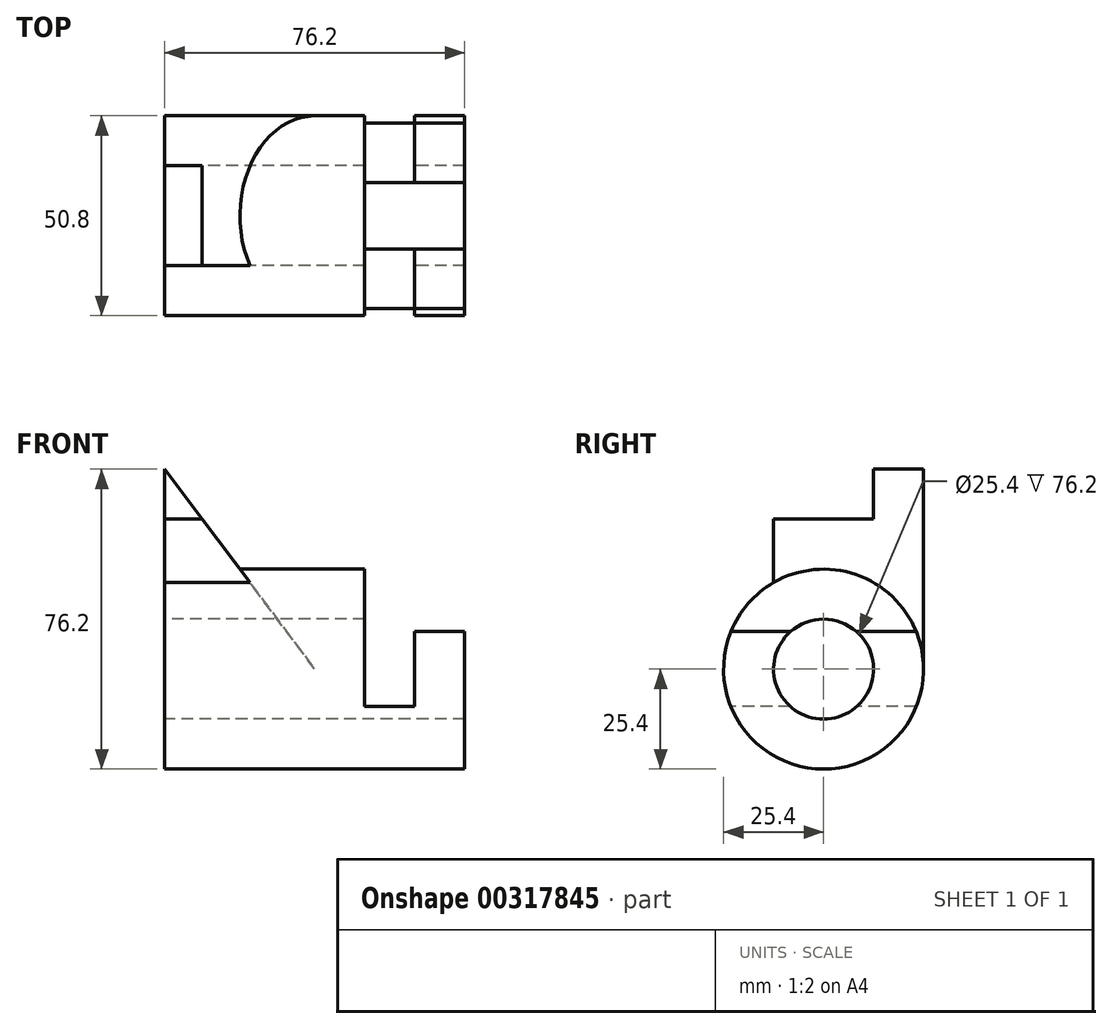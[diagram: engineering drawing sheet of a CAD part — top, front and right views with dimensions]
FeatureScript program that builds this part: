
annotation { "Feature Type Name" : "Feature", "Feature Type Description" : "" }
export const myFeature = defineFeature(function(context is Context, id is Id, definition is map)
    precondition{}
    {
        {
            var Q0;
            Q0=qCreatedBy(makeId("Right.planeOp"),FACE);
            var sketch = newSketch(context, id + "F0", { "sketchPlane" : qUnion([Q0])});
            skCircle(sketch, "E0", {"center": v(0, 0) * mm, "radius": 25.4 * mm});
            skCircle(sketch, "E1", {"center": v(0, 0) * mm, "radius": 12.7 * mm});
            skSolve(sketch);
        }
        {
            var Q0;
            Q0 = qSketchRegion(id + "F0", true);
            extrude(context, id + "F1", {"entities" : qUnion([Q0]), "depth" : 76.2 * mm});
        }
        {
            var Q0;
            Q0=makeQuery(id+"F1.opExtrude","CAP_FACE",FACE,{"disambiguationData":[OSD([sQuery(id+"F0.wireOp",EDGE,"E0"),sQuery(id+"F0.wireOp",EDGE,"E1")])],"isStart":false});
            var sketch = newSketch(context, id + "F2", { "sketchPlane" : qUnion([Q0])});
            skLineSegment(sketch, "E2.bottom", {"start": v(-25.4, 25.4) * mm, "end": v(25.4, 25.4) * mm});
            skLineSegment(sketch, "E2.top", {"start": v(-25.4, 9.53) * mm, "end": v(25.4, 9.53) * mm});
            skLineSegment(sketch, "E2.left", {"start": v(-25.4, 25.4) * mm, "end": v(-25.4, 9.52) * mm});
            skLineSegment(sketch, "E2.right", {"start": v(25.4, 25.4) * mm, "end": v(25.4, 9.53) * mm});
            skSolve(sketch);
        }
        {
            var Q0;
            Q0 = qSketchRegion(id + "F2", true);
            extrude(context, id + "F3", {"entities" : qUnion([Q0]), "operationType" : NewBodyOperationType.REMOVE, "oppositeDirection" : true, "depth" : 25.4 * mm});
        }
        {
            var Q0;
            Q0=qCreatedBy(makeId("Front.planeOp"),FACE);
            var sketch = newSketch(context, id + "F4", { "sketchPlane" : qUnion([Q0])});
            skLineSegment(sketch, "E3.bottom", {"start": v(50.8, 25.4) * mm, "end": v(63.5, 25.4) * mm});
            skLineSegment(sketch, "E3.top", {"start": v(50.8, -9.53) * mm, "end": v(63.5, -9.53) * mm});
            skLineSegment(sketch, "E3.left", {"start": v(50.8, 25.4) * mm, "end": v(50.8, -9.52) * mm});
            skLineSegment(sketch, "E3.right", {"start": v(63.5, 25.4) * mm, "end": v(63.5, -9.52) * mm});
            skSolve(sketch);
        }
        {
            var Q0;
            Q0 = qSketchRegion(id + "F4", true);
            extrude(context, id + "F5", {"entities" : qUnion([Q0]), "operationType" : NewBodyOperationType.REMOVE, "endBound" : BoundingType.THROUGH_ALL, "oppositeDirection" : true, "depth" : 25.4 * mm, "hasSecondDirection" : true, "secondDirectionBound" : SecondDirectionBoundingType.THROUGH_ALL, "secondDirectionOppositeDirection" : false, "secondDirectionDepth" : 25.4 * mm});
        }
        {
            var Q0;
            Q0=qCreatedBy(makeId("Front.planeOp"),FACE);
            var sketch = newSketch(context, id + "F6", { "sketchPlane" : qUnion([Q0])});
            skLineSegment(sketch, "E4", {"start": v(0, 50.8) * mm, "end": v(0, 0) * mm});
            skLineSegment(sketch, "E5", {"start": v(0, 0) * mm, "end": v(38.1, 0) * mm});
            skLineSegment(sketch, "E6", {"start": v(38.1, 0) * mm, "end": v(0, 50.8) * mm});
            skSolve(sketch);
        }
        {
            var Q0;
            Q0 = qSketchRegion(id + "F6", true);
            extrude(context, id + "F7", {"entities" : qUnion([Q0]), "operationType" : NewBodyOperationType.ADD, "depth" : 12.7 * mm, "hasSecondDirection" : true, "secondDirectionOppositeDirection" : true, "secondDirectionDepth" : 25.4 * mm});
        }
        {
            var Q0;
            Q0=qCreatedBy(makeId("Right.planeOp"),FACE);
            var sketch = newSketch(context, id + "F8", { "sketchPlane" : qUnion([Q0])});
            skCircle(sketch, "E7", {"center": v(0, 0) * mm, "radius": 12.7 * mm});
            skSolve(sketch);
        }
        {
            var Q0;
            Q0=makeQuery(id+"F8.imprint","IMPRINT",FACE,{"disambiguationData":[TD([[makeQuery(id+"F8.imprint","IMPRINT",EDGE,{"derivedFrom":sQuery(id+"F8.wireOp",EDGE,"E7")}),1.0]])]});
            extrude(context, id + "F9", {"entities" : qUnion([Q0]), "operationType" : NewBodyOperationType.REMOVE, "endBound" : BoundingType.THROUGH_ALL, "depth" : 25.4 * mm});
        }
        {
            var Q0;
            Q0=qCreatedBy(makeId("Right.planeOp"),FACE);
            var sketch = newSketch(context, id + "F10", { "sketchPlane" : qUnion([Q0])});
            skLineSegment(sketch, "E8.bottom", {"start": v(-12.7, 50.8) * mm, "end": v(12.7, 50.8) * mm});
            skLineSegment(sketch, "E8.top", {"start": v(-12.7, 38.1) * mm, "end": v(12.7, 38.1) * mm});
            skLineSegment(sketch, "E8.left", {"start": v(-12.7, 50.8) * mm, "end": v(-12.7, 38.1) * mm});
            skLineSegment(sketch, "E8.right", {"start": v(12.7, 50.8) * mm, "end": v(12.7, 38.1) * mm});
            skSolve(sketch);
        }
        {
            var Q0;
            Q0 = qSketchRegion(id + "F10", true);
            extrude(context, id + "F11", {"entities" : qUnion([Q0]), "operationType" : NewBodyOperationType.REMOVE, "endBound" : BoundingType.THROUGH_ALL, "depth" : 25.4 * mm});
        }
    });
